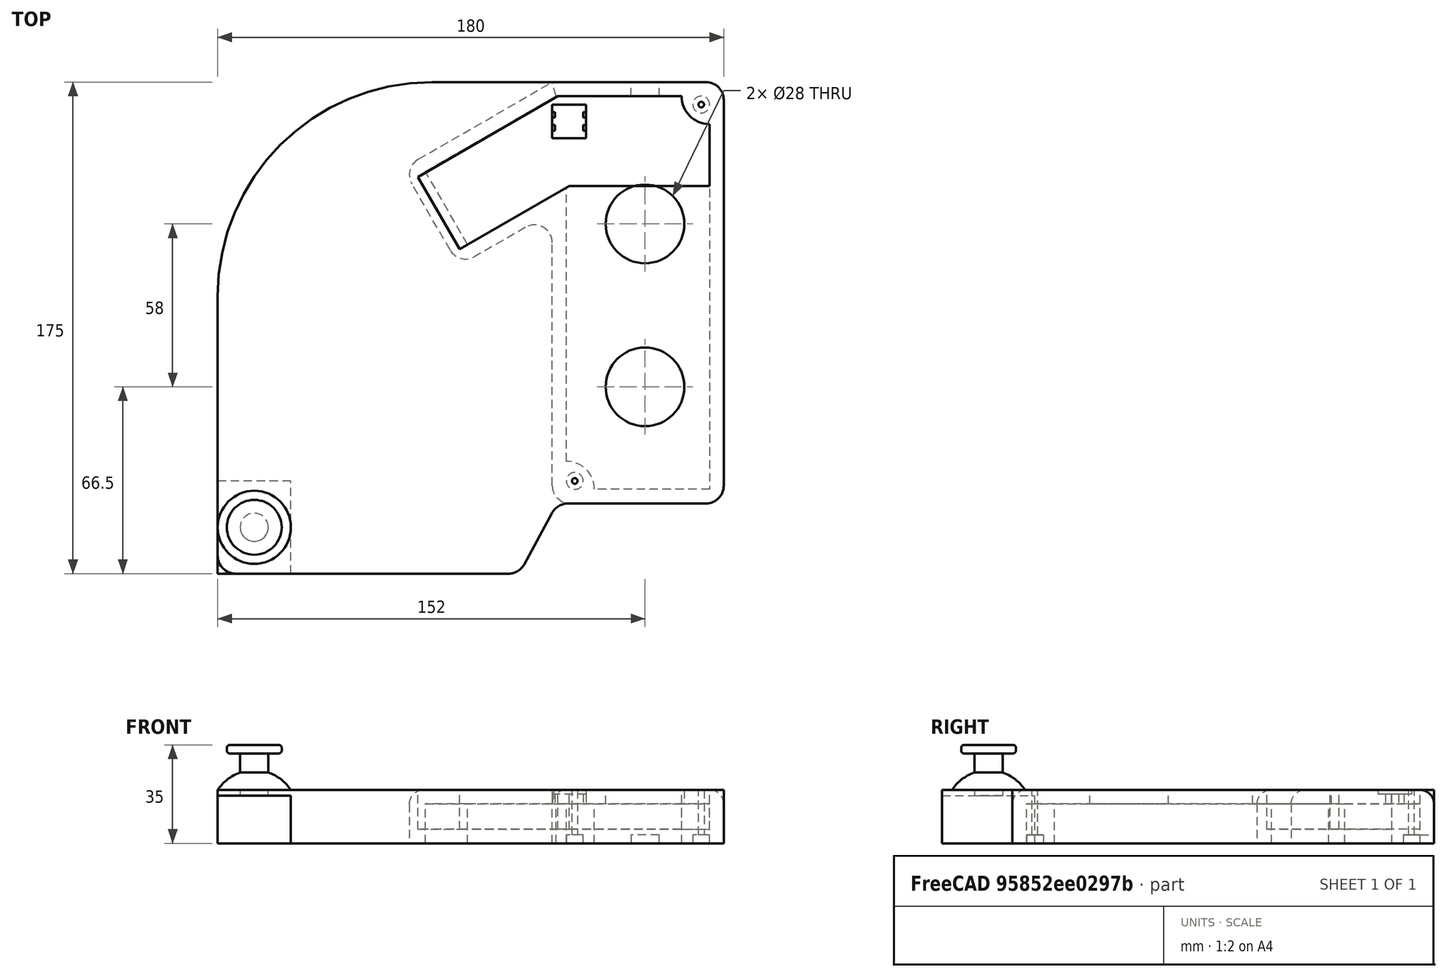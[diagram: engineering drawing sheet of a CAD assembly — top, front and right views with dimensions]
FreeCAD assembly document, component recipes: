
FREECAD ASSEMBLY — COMPONENT RECIPES ("base1")

This assembly document has 3 components, labeled P0..P2 below (a component is one placed body or linked part). 3 of them carry a construction recipe — the FreeCAD feature program that regenerates the part from scratch, quoted from this document or its linked companion documents; the rest are supplied as boundary geometry only. No exploded tour is included for this assembly.
COMPONENT P0 — recipe-attached ("BasePlate", modeled in this document).
Construction recipe (the document's own serialized feature program — sketch geometry with constraints, then the solid features built on it; lengths are millimeters unless a unit is written):

FEATURE [Sketcher::SketchObject] Sketch  label="Base_Ref"
  MapMode = 5
  Support = -> [XY_Plane]
  expr: Constraints[9] = vars.base_l
  expr: Constraints[10] = vars.base_w
  sketch-geometry (4):
    g0: LineSegment StartX=0 StartY=175 StartZ=0 EndX=180 EndY=175 EndZ=0
    g1: LineSegment StartX=180 StartY=175 StartZ=0 EndX=180 EndY=0 EndZ=0
    g2: LineSegment StartX=180 StartY=0 StartZ=0 EndX=0 EndY=0 EndZ=0
    g3: LineSegment StartX=0 StartY=0 StartZ=0 EndX=0 EndY=175 EndZ=0
  constraints (11):
    c: Coincident(g0,g1)
    c: Coincident(g1,g2)
    c: Coincident(g2,g3)
    c: Coincident(g3,g0)
    c: Horizontal(g0)
    c: Horizontal(g2)
    c: Vertical(g1)
    c: Vertical(g3)
    c: Coincident(g2,g-1)
    c: DistanceY(g1,g1) = 175
    c: DistanceX(g0,g0) = 180
FEATURE [Sketcher::SketchObject] Sketch001  label="Base"
  ExternalGeometry = -> [Sketch]
  MapMode = 5
  Support = -> [XY_Plane]
  expr: Constraints[6] = vars.round
  expr: Constraints[10] = vars.round
  expr: Constraints[17] = vars.big_round
  expr: Constraints[22] = vars.round
  expr: Constraints[23] = vars.round
  expr: Constraints[24] = vars.joystick1_margin_out - vars.joystick1_margin_in
  expr: Constraints[25] = vars.joystick1_margin_right + vars.joystick_w + vars.joystick1_margin_left
  sketch-geometry (11):
    g0: LineSegment StartX=180 StartY=175 StartZ=0 EndX=180 EndY=31.35 EndZ=0
    g1: LineSegment StartX=173.65 StartY=25 StartZ=0 EndX=124.577 EndY=25 EndZ=0
    g2: LineSegment StartX=119 StartY=21.6858 StartZ=0 EndX=109 EndY=3.31418 EndZ=0
    g3: LineSegment StartX=103.423 StartY=0 StartZ=0 EndX=6.35 EndY=0 EndZ=0
    g4: ArcOfCircle CenterX=124.577 CenterY=18.65 CenterZ=0 NormalX=0 NormalY=0 NormalZ=1 AngleXU=0 Radius=6.35 StartAngle=1.5708 EndAngle=2.64312
    g5: ArcOfCircle CenterX=103.423 CenterY=6.35 CenterZ=0 NormalX=0 NormalY=0 NormalZ=1 AngleXU=0 Radius=6.35 StartAngle=4.71239 EndAngle=5.78472
    g6: LineSegment StartX=180 StartY=175 StartZ=0 EndX=76.2 EndY=175 EndZ=0
    g7: LineSegment StartX=0 StartY=98.8 StartZ=0 EndX=0 EndY=6.35 EndZ=0
    g8: ArcOfCircle CenterX=76.2 CenterY=98.8 CenterZ=0 NormalX=0 NormalY=0 NormalZ=1 AngleXU=0 Radius=76.2 StartAngle=1.5708 EndAngle=3.14159
    g9: ArcOfCircle CenterX=173.65 CenterY=31.35 CenterZ=0 NormalX=0 NormalY=0 NormalZ=1 AngleXU=0 Radius=6.35 StartAngle=4.71239 EndAngle=6.28319
    g10: ArcOfCircle CenterX=6.35 CenterY=6.35 CenterZ=0 NormalX=0 NormalY=0 NormalZ=1 AngleXU=0 Radius=6.35 StartAngle=3.14159 EndAngle=4.71239
  constraints (27):
    c: Coincident(g-3,g0)
    c: Vertical(g0)
    c: Horizontal(g1)
    c: PointOnObject(g3,g-5)
    c: Tangent(g4,g1) = -1.5708
    c: Tangent(g4,g2) = -1.5708
    c: Radius(g4) = 6.35
    c: PointOnObject(g3,g-5)
    c: Tangent(g5,g2) = 1.5708
    c: Tangent(g5,g3) = 1.5708
    c: Radius(g5) = 6.35
    c: Coincident(g6,g0)
    c: Horizontal(g6)
    c: PointOnObject(g7,g-4)
    c: PointOnObject(g7,g-4)
    c: Tangent(g8,g6) = -1.5708
    c: Tangent(g8,g7) = -1.5708
    c: Radius(g8) = 76.2
    c: Tangent(g9,g0) = 1.5708
    c: Tangent(g9,g1) = 1.5708
    c: Tangent(g10,g3) = 1.5708
    c: Tangent(g10,g7) = -1.5708
    c: Radius(g10) = 6.35
    c: Radius(g9) = 6.35
    c: DistanceY(g-5,g1) = 25
    c: DistanceX(g2,g0) = 61
    c: DistanceX(g2,g2) = 10
FEATURE [PartDesign::Pad] Pad
  Length = 19
  Length2 = 100
  Profile = -> Sketch001
  Type = 0
  expr: Length = vars.base_t
FEATURE [PartDesign::CoordinateSystem] LCS_1
  AttacherType = Attacher::AttachEngine3D
  MapMode = 7
  Placement = pos=(180,0,0) rot=(0,0.707107,0.707107;3.14159rad)
  Support = -> [Sketch]
FEATURE [PartDesign::Fillet] Fillet001
  Base = -> Pad [Edge1]
  BaseFeature = -> Pad
  Radius = 6.35
  SupportTransform = true
  expr: Radius = vars.round
FEATURE [Sketcher::SketchObject] Sketch007
  AttachmentOffset = pos=(0,0,5) rot=(0,0,1;0rad)
  ExternalGeometry = -> [Sketch]
  MapMode = 5
  Placement = pos=(0,0,5) rot=(0,0,1;0rad)
  Support = -> [XY_Plane]
  expr: Constraints[12] = vars.top_wall
  expr: .AttachmentOffset.Base.z = vars.top_wall
  expr: Constraints[11] = vars.top_wall
  expr: Constraints[5] = 22
  expr: Constraints[19] = vars.buttons_angle + 90
  expr: Constraints[20] = 45
  sketch-geometry (7):
    g0: LineSegment StartX=165 StartY=170 StartZ=0 EndX=121 EndY=170 EndZ=0
    g1: LineSegment StartX=125 StartY=138 StartZ=0 EndX=175 EndY=138 EndZ=0
    g2: LineSegment StartX=175 StartY=138 StartZ=0 EndX=175 EndY=160 EndZ=0
    g3: ArcOfCircle CenterX=175 CenterY=170 CenterZ=0 NormalX=0 NormalY=0 NormalZ=1 AngleXU=0 Radius=10 StartAngle=3.14159 EndAngle=4.71239
    g4: LineSegment StartX=121 StartY=170 StartZ=0 EndX=71.1725 EndY=141.232 EndZ=0
    g5: LineSegment StartX=71.1725 StartY=141.232 StartZ=0 EndX=86.0289 EndY=115.5 EndZ=0
    g6: LineSegment StartX=86.0289 StartY=115.5 StartZ=0 EndX=125 EndY=138 EndZ=0
  constraints (22):
    c: Coincident(g1,g2)
    c: Horizontal(g0)
    c: Horizontal(g1)
    c: Vertical(g2)
    c: DistanceX(g1,g1) = 50
    c: DistanceY(g2,g2) = 22
    c: Coincident(g3,g0)
    c: Coincident(g3,g2)
    c: PointOnObject(g3,g0)
    c: PointOnObject(g3,g2)
    c: Radius(g3) = 10
    c: DistanceX(g2,g-3) = 5
    c: DistanceY(g0,g-3) = 5
    c: Coincident(g0,g4)
    c: Coincident(g4,g5)
    c: Coincident(g5,g6)
    c: Coincident(g6,g1)
    c: Parallel(g6,g4)
    c: Perpendicular(g5,g4)
    c: Angle(g4,g0) = 2.61799
    c: Distance(g6) = 45
    c: DistanceX(g0,g0) = 44
FEATURE [PartDesign::Pocket] Pocket002
  BaseFeature = -> Fillet001
  Length = 5
  Length2 = 100
  Profile = -> Sketch007
  Reversed = true
  Type = 1
FEATURE [PartDesign::CoordinateSystem] LCS_7
  AttacherType = Attacher::AttachEngine3D
  MapMode = 7
  Placement = pos=(86.0289,115.5,5) rot=(0.774597,-0.447214,-0.447214;1.82348rad)
  Support = -> [Sketch007]
FEATURE [Sketcher::SketchObject] Sketch014
  ExternalGeometry = -> [Sketch001]
  MapMode = 5
  Support = -> [XY_Plane]
  sketch-geometry (2):
    g0: Circle CenterX=172 CenterY=167 CenterZ=0 NormalX=0 NormalY=0 NormalZ=1 AngleXU=0 Radius=1
    g1: Circle CenterX=127 CenterY=33 CenterZ=0 NormalX=0 NormalY=0 NormalZ=1 AngleXU=0 Radius=1
  constraints (6):
    c: DistanceY(g0,g-4) = 8
    c: DistanceX(g0,g-4) = 8
    c: Radius(g0) = 1
    c: DistanceY(g-5,g1) = 8
    c: DistanceX(g-6,g1) = 8
    c: Equal(g1,g0)
FEATURE [PartDesign::Pocket] Pocket005
  BaseFeature = -> Pocket002
  Length = 5
  Length2 = 100
  Midplane = true
  Profile = -> Sketch014
  Type = 1
FEATURE [Sketcher::SketchObject] Sketch015
  ExternalGeometry = -> [Sketch014]
  MapMode = 5
  Support = -> [XY_Plane]
  sketch-geometry (2):
    g0: Circle CenterX=127 CenterY=33 CenterZ=0 NormalX=0 NormalY=0 NormalZ=1 AngleXU=0 Radius=3
    g1: Circle CenterX=172 CenterY=167 CenterZ=0 NormalX=0 NormalY=0 NormalZ=1 AngleXU=0 Radius=3
  constraints (4):
    c: Coincident(g-4,g0)
    c: Coincident(g1,g-3)
    c: Equal(g1,g0)
    c: Radius(g1) = 3
FEATURE [PartDesign::Pocket] Pocket006
  BaseFeature = -> Pocket005
  Length = 3
  Length2 = 100
  Profile = -> Sketch015
  Reversed = true
  Type = 0
FEATURE [PartDesign::Body] Body  label="BasePlate"
  Group = -> [Sketch,Sketch001,Pad,LCS_1,Fillet001,Sketch007,Pocket002,LCS_7,Sketch014,Pocket005,Sketch015,Pocket006]
  Origin = -> Origin
  Tip = -> Pocket006
COMPONENT P1 — recipe-attached ("TopPlate", modeled in this document).
Construction recipe (the document's own serialized feature program — sketch geometry with constraints, then the solid features built on it; lengths are millimeters unless a unit is written):

FEATURE [Sketcher::SketchObject] Sketch002  label="Base_Ref001"
  MapMode = 5
  Support = -> [XY_Plane001]
  expr: Constraints[10] = vars.base_w
  expr: Constraints[9] = vars.base_l
  sketch-geometry (4):
    g0: LineSegment StartX=0 StartY=175 StartZ=0 EndX=180 EndY=175 EndZ=0
    g1: LineSegment StartX=180 StartY=175 StartZ=0 EndX=180 EndY=0 EndZ=0
    g2: LineSegment StartX=180 StartY=0 StartZ=0 EndX=0 EndY=0 EndZ=0
    g3: LineSegment StartX=0 StartY=0 StartZ=0 EndX=0 EndY=175 EndZ=0
  constraints (11):
    c: Coincident(g0,g1)
    c: Coincident(g1,g2)
    c: Coincident(g2,g3)
    c: Coincident(g3,g0)
    c: Horizontal(g0)
    c: Horizontal(g2)
    c: Vertical(g1)
    c: Vertical(g3)
    c: Coincident(g2,g-1)
    c: DistanceY(g1,g1) = 175
    c: DistanceX(g0,g0) = 180
FEATURE [Sketcher::SketchObject] Sketch003  label="Base001"
  ExternalGeometry = -> [Sketch002]
  MapMode = 5
  Support = -> [XY_Plane001]
  expr: Constraints[25] = vars.joystick1_margin_right + vars.joystick_w + vars.joystick1_margin_left
  expr: Constraints[24] = vars.joystick1_margin_out - vars.joystick1_margin_in
  expr: Constraints[23] = vars.round
  expr: Constraints[22] = vars.round
  expr: Constraints[17] = vars.big_round
  expr: Constraints[10] = vars.round
  expr: Constraints[6] = vars.round
  sketch-geometry (11):
    g0: LineSegment StartX=180 StartY=175 StartZ=0 EndX=180 EndY=31.35 EndZ=0
    g1: LineSegment StartX=173.65 StartY=25 StartZ=0 EndX=124.577 EndY=25 EndZ=0
    g2: LineSegment StartX=119 StartY=21.6858 StartZ=0 EndX=109 EndY=3.31418 EndZ=0
    g3: LineSegment StartX=103.423 StartY=0 StartZ=0 EndX=6.35 EndY=0 EndZ=0
    g4: ArcOfCircle CenterX=124.577 CenterY=18.65 CenterZ=0 NormalX=0 NormalY=0 NormalZ=1 AngleXU=0 Radius=6.35 StartAngle=1.5708 EndAngle=2.64312
    g5: ArcOfCircle CenterX=103.423 CenterY=6.35 CenterZ=0 NormalX=0 NormalY=0 NormalZ=1 AngleXU=0 Radius=6.35 StartAngle=4.71239 EndAngle=5.78472
    g6: LineSegment StartX=180 StartY=175 StartZ=0 EndX=76.2 EndY=175 EndZ=0
    g7: LineSegment StartX=0 StartY=98.8 StartZ=0 EndX=0 EndY=6.35 EndZ=0
    g8: ArcOfCircle CenterX=76.2 CenterY=98.8 CenterZ=0 NormalX=0 NormalY=0 NormalZ=1 AngleXU=0 Radius=76.2 StartAngle=1.5708 EndAngle=3.14159
    g9: ArcOfCircle CenterX=173.65 CenterY=31.35 CenterZ=0 NormalX=0 NormalY=0 NormalZ=1 AngleXU=0 Radius=6.35 StartAngle=4.71239 EndAngle=6.28319
    g10: ArcOfCircle CenterX=6.35 CenterY=6.35 CenterZ=0 NormalX=0 NormalY=0 NormalZ=1 AngleXU=0 Radius=6.35 StartAngle=3.14159 EndAngle=4.71239
  constraints (27):
    c: Coincident(g-3,g0)
    c: Vertical(g0)
    c: Horizontal(g1)
    c: PointOnObject(g3,g-5)
    c: Tangent(g4,g1) = -1.5708
    c: Tangent(g4,g2) = -1.5708
    c: Radius(g4) = 6.35
    c: PointOnObject(g3,g-5)
    c: Tangent(g5,g2) = 1.5708
    c: Tangent(g5,g3) = 1.5708
    c: Radius(g5) = 6.35
    c: Coincident(g6,g0)
    c: Horizontal(g6)
    c: PointOnObject(g7,g-4)
    c: PointOnObject(g7,g-4)
    c: Tangent(g8,g6) = -1.5708
    c: Tangent(g8,g7) = -1.5708
    c: Radius(g8) = 76.2
    c: Tangent(g9,g0) = 1.5708
    c: Tangent(g9,g1) = 1.5708
    c: Tangent(g10,g3) = 1.5708
    c: Tangent(g10,g7) = -1.5708
    c: Radius(g10) = 6.35
    c: Radius(g9) = 6.35
    c: DistanceY(g-5,g1) = 25
    c: DistanceX(g2,g0) = 61
    c: DistanceX(g2,g2) = 10
FEATURE [Sketcher::SketchObject] Sketch004
  ExternalGeometry = -> [Sketch002]
  MapMode = 5
  Support = -> [XY_Plane001]
  expr: Constraints[18] = vars.joystick_sep
  expr: Constraints[19] = vars.joystick1_margin_right
  expr: Constraints[23] = vars.joystick_w
  expr: Constraints[20] = vars.joystick1_margin_out
  expr: Constraints[22] = vars.joystick_l
  expr: Constraints[25] = vars.joystick_w / 2 + 1
  sketch-geometry (11):
    g0: LineSegment [constr] StartX=139 StartY=83 StartZ=0 EndX=165 EndY=83 EndZ=0
    g1: LineSegment [constr] StartX=165 StartY=83 StartZ=0 EndX=165 EndY=50 EndZ=0
    g2: LineSegment [constr] StartX=165 StartY=50 StartZ=0 EndX=139 EndY=50 EndZ=0
    g3: LineSegment [constr] StartX=139 StartY=50 StartZ=0 EndX=139 EndY=83 EndZ=0
    g4: LineSegment [constr] StartX=139 StartY=141 StartZ=0 EndX=165 EndY=141 EndZ=0
    g5: LineSegment [constr] StartX=165 StartY=141 StartZ=0 EndX=165 EndY=108 EndZ=0
    g6: LineSegment [constr] StartX=165 StartY=108 StartZ=0 EndX=139 EndY=108 EndZ=0
    g7: LineSegment [constr] StartX=139 StartY=108 StartZ=0 EndX=139 EndY=141 EndZ=0
    g8: Circle CenterX=152 CenterY=124.5 CenterZ=0 NormalX=0 NormalY=0 NormalZ=1 AngleXU=0 Radius=14
    g9: GeomPoint X=152 Y=66.5 Z=0
    g10: Circle CenterX=152 CenterY=66.5 CenterZ=0 NormalX=0 NormalY=0 NormalZ=1 AngleXU=0 Radius=14
  constraints (29):
    c: Coincident(g0,g1)
    c: Coincident(g1,g2)
    c: Coincident(g2,g3)
    c: Coincident(g3,g0)
    c: Horizontal(g0)
    c: Horizontal(g2)
    c: Vertical(g1)
    c: Vertical(g3)
    c: Coincident(g4,g5)
    c: Coincident(g5,g6)
    c: Coincident(g6,g7)
    c: Coincident(g7,g4)
    c: Horizontal(g4)
    c: Horizontal(g6)
    c: Vertical(g5)
    c: Vertical(g7)
    c: PointOnObject(g6,g3)
    c: PointOnObject(g5,g1)
    c: DistanceY(g0,g5) = 25
    c: DistanceX(g1,g-3) = 15
    c: DistanceY(g-3,g1) = 50
    c: Equal(g5,g1)
    c: DistanceY(g1,g1) = 33
    c: DistanceX(g4,g4) = 26
    c: Symmetric(g5,g4,g8)
    c: Radius(g8) = 14
    c: Symmetric(g0,g1,g9)
    c: Coincident(g10,g9)
    c: Equal(g10,g8)
FEATURE [PartDesign::CoordinateSystem] LCS_2
  AttacherType = Attacher::AttachEngine3D
  MapMode = 7
  Placement = pos=(180,0,0) rot=(0,0.707107,0.707107;3.14159rad)
  Support = -> [Sketch002]
FEATURE [Sketcher::SketchObject] Sketch005
  ExternalGeometry = -> [Sketch002]
  MapMode = 5
  Support = -> [XY_Plane001]
  expr: Constraints[56] = vars.buttons_l
  expr: Constraints[46] = vars.buttons_angle
  expr: Constraints[32] = vars.joystick1_margin_out - vars.joystick1_margin_in
  expr: Constraints[28] = vars.round
  expr: Constraints[55] = vars.buttons_w
  expr: Constraints[22] = vars.joystick_l
  expr: Constraints[20] = vars.joystick1_margin_out
  expr: Constraints[23] = vars.joystick_w
  expr: Constraints[19] = vars.joystick1_margin_right
  expr: Constraints[36] = vars.joystick1_margin_left
  expr: Constraints[18] = vars.joystick_sep
  sketch-geometry (21):
    g0: LineSegment [constr] StartX=139 StartY=83 StartZ=0 EndX=165 EndY=83 EndZ=0
    g1: LineSegment [constr] StartX=165 StartY=83 StartZ=0 EndX=165 EndY=50 EndZ=0
    g2: LineSegment [constr] StartX=165 StartY=50 StartZ=0 EndX=139 EndY=50 EndZ=0
    g3: LineSegment [constr] StartX=139 StartY=50 StartZ=0 EndX=139 EndY=83 EndZ=0
    g4: LineSegment [constr] StartX=139 StartY=141 StartZ=0 EndX=165 EndY=141 EndZ=0
    g5: LineSegment [constr] StartX=165 StartY=141 StartZ=0 EndX=165 EndY=108 EndZ=0
    g6: LineSegment [constr] StartX=165 StartY=108 StartZ=0 EndX=139 EndY=108 EndZ=0
    g7: LineSegment [constr] StartX=139 StartY=108 StartZ=0 EndX=139 EndY=141 EndZ=0
    g8: LineSegment StartX=119 StartY=31.35 StartZ=0 EndX=119 EndY=117.813 EndZ=0
    g9: LineSegment StartX=109.475 StartY=123.313 StartZ=0 EndX=91.3686 EndY=112.859 EndZ=0
    g10: LineSegment StartX=82.6943 StartY=115.183 StartZ=0 EndX=69.0443 EndY=138.826 EndZ=0
    g11: LineSegment StartX=71.3686 StartY=147.5 StartZ=0 EndX=119 EndY=175 EndZ=0
    g12: LineSegment StartX=119 StartY=175 StartZ=0 EndX=173.65 EndY=175 EndZ=0
    g13: LineSegment StartX=180 StartY=168.65 StartZ=0 EndX=180 EndY=31.35 EndZ=0
    g14: LineSegment StartX=173.65 StartY=25 StartZ=0 EndX=125.35 EndY=25 EndZ=0
    g15: ArcOfCircle CenterX=173.65 CenterY=31.35 CenterZ=0 NormalX=0 NormalY=0 NormalZ=1 AngleXU=0 Radius=6.35 StartAngle=4.71239 EndAngle=6.28319
    g16: ArcOfCircle CenterX=125.35 CenterY=31.35 CenterZ=0 NormalX=0 NormalY=0 NormalZ=1 AngleXU=0 Radius=6.35 StartAngle=3.14159 EndAngle=4.71239
    g17: ArcOfCircle CenterX=112.65 CenterY=117.813 CenterZ=0 NormalX=0 NormalY=0 NormalZ=1 AngleXU=0 Radius=6.35 StartAngle=7e-16 EndAngle=2.0944
    g18: ArcOfCircle CenterX=88.1936 CenterY=118.358 CenterZ=0 NormalX=0 NormalY=0 NormalZ=1 AngleXU=0 Radius=6.35 StartAngle=3.66519 EndAngle=5.23599
    g19: ArcOfCircle CenterX=74.5436 CenterY=142.001 CenterZ=0 NormalX=0 NormalY=0 NormalZ=1 AngleXU=0 Radius=6.35 StartAngle=2.0944 EndAngle=3.66519
    g20: ArcOfCircle CenterX=173.65 CenterY=168.65 CenterZ=0 NormalX=0 NormalY=0 NormalZ=1 AngleXU=0 Radius=6.35 StartAngle=3e-16 EndAngle=1.5708
  constraints (57):
    c: Coincident(g0,g1)
    c: Coincident(g1,g2)
    c: Coincident(g2,g3)
    c: Coincident(g3,g0)
    c: Horizontal(g0)
    c: Horizontal(g2)
    c: Vertical(g1)
    c: Vertical(g3)
    c: Coincident(g4,g5)
    c: Coincident(g5,g6)
    c: Coincident(g6,g7)
    c: Coincident(g7,g4)
    c: Horizontal(g4)
    c: Horizontal(g6)
    c: Vertical(g5)
    c: Vertical(g7)
    c: PointOnObject(g6,g3)
    c: PointOnObject(g5,g1)
    c: DistanceY(g0,g5) = 25
    c: DistanceX(g1,g-3) = 15
    c: DistanceY(g-3,g1) = 50
    c: Equal(g5,g1)
    c: DistanceY(g1,g1) = 33
    c: DistanceX(g4,g4) = 26
    c: Vertical(g8)
    c: Horizontal(g12)
    c: Tangent(g15,g13) = 1.5708
    c: Tangent(g15,g14) = 1.5708
    c: Radius(g15) = 6.35
    c: Horizontal(g14)
    c: Vertical(g13)
    c: PointOnObject(g-3,g13)
    c: DistanceY(g-3,g14) = 25
    c: Tangent(g16,g14) = 1.5708
    c: Tangent(g16,g8) = 1.5708
    c: Equal(g16,g15)
    c: DistanceX(g8,g2) = 20
    c: Tangent(g17,g8) = -1.5708
    c: Tangent(g17,g9) = -1.5708
    c: Tangent(g19,g11) = 1.5708
    c: Tangent(g18,g9) = 1.5708
    c: Tangent(g18,g10) = 1.5708
    c: Equal(g16,g17)
    c: Equal(g17,g18)
    c: Equal(g18,g19)
    c: Parallel(g11,g9)
    c: Angle(g9,g8) = 1.0472
    c: Perpendicular(g9,g10)
    c: Tangent(g20,g13) = 1.5708
    c: Tangent(g20,g12) = 1.5708
    c: Equal(g16,g20)
    c: Coincident(g11,g12)
    c: PointOnObject(g11,g8)
    c: PointOnObject(g11,g-4)
    c: Tangent(g10,g19) = 1.5708
    c: Distance(g9,g11) = 40
    c: Distance(g11) = 55
FEATURE [PartDesign::Pad] Pad001
  Length = 19
  Length2 = 100
  Profile = -> Sketch005
  Type = 0
  expr: Length = vars.base_t
FEATURE [PartDesign::Pocket] Pocket
  BaseFeature = -> Pad001
  Length = 5
  Length2 = 100
  Midplane = true
  Profile = -> Sketch004
  Type = 1
FEATURE [Sketcher::SketchObject] Sketch006
  ExternalGeometry = -> [Sketch005]
  MapMode = 5
  Support = -> [XY_Plane001]
  expr: Constraints[11] = vars.top_wall
  expr: Constraints[16] = vars.buttons_w - 2 * vars.top_wall
  expr: Constraints[12] = vars.top_wall
  expr: Constraints[10] = vars.top_wall
  expr: Constraints[32] = vars.top_wall
  sketch-geometry (11):
    g0: LineSegment StartX=73.8686 StartY=143.17 StartZ=0 EndX=120.34 EndY=170 EndZ=0
    g1: LineSegment StartX=120.34 StartY=170 StartZ=0 EndX=165 EndY=170 EndZ=0
    g2: LineSegment StartX=175 StartY=160 StartZ=0 EndX=175 EndY=30 EndZ=0
    g3: LineSegment StartX=175 StartY=30 StartZ=0 EndX=134 EndY=30 EndZ=0
    g4: LineSegment StartX=124 StartY=40 StartZ=0 EndX=124 EndY=137.472 EndZ=0
    g5: LineSegment StartX=124 StartY=137.472 StartZ=0 EndX=88.8686 EndY=117.189 EndZ=0
    g6: LineSegment StartX=88.8686 StartY=117.189 StartZ=0 EndX=73.8686 EndY=143.17 EndZ=0
    g7: LineSegment [constr] StartX=71.3686 StartY=147.5 StartZ=0 EndX=73.8686 EndY=143.17 EndZ=0
    g8: LineSegment [constr] StartX=88.8686 StartY=117.189 StartZ=0 EndX=91.3686 EndY=112.859 EndZ=0
    g9: ArcOfCircle CenterX=175 CenterY=170 CenterZ=0 NormalX=0 NormalY=0 NormalZ=1 AngleXU=0 Radius=10 StartAngle=3.14159 EndAngle=4.71239
    g10: ArcOfCircle CenterX=124 CenterY=30 CenterZ=0 NormalX=0 NormalY=0 NormalZ=1 AngleXU=0 Radius=10 StartAngle=-9e-16 EndAngle=1.5708
  constraints (33):
    c: Coincident(g0,g1)
    c: Horizontal(g1)
    c: Vertical(g2)
    c: Coincident(g2,g3)
    c: Vertical(g4)
    c: Coincident(g4,g5)
    c: Coincident(g5,g6)
    c: Parallel(g-3,g3)
    c: Parallel(g5,g-8)
    c: Parallel(g6,g-9)
    c: DistanceY(g-3,g2) = 5
    c: DistanceX(g2,g-5) = 5
    c: DistanceY(g1,g-6) = 5
    c: Coincident(g0,g6)
    c: Parallel(g0,g-7)
    c: PointOnObject(g-7,g6)
    c: Distance(g6) = 30
    c: Coincident(g7,g-7)
    c: Coincident(g7,g0)
    c: Coincident(g8,g5)
    c: Coincident(g8,g-8)
    c: Equal(g8,g7)
    c: Coincident(g9,g1)
    c: Coincident(g9,g2)
    c: Radius(g9) = 10
    c: PointOnObject(g9,g1)
    c: PointOnObject(g9,g2)
    c: Coincident(g10,g4)
    c: Coincident(g10,g3)
    c: Equal(g9,g10)
    c: PointOnObject(g10,g4)
    c: PointOnObject(g10,g3)
    c: DistanceX(g-4,g10) = 5
FEATURE [PartDesign::Pocket] Pocket001
  BaseFeature = -> Pocket
  Length = 14
  Length2 = 100
  Profile = -> Sketch006
  Reversed = true
  Type = 0
  expr: Length = vars.base_t - vars.top_wall
FEATURE [PartDesign::Fillet] Fillet
  Base = -> Pocket001 [Edge31]
  BaseFeature = -> Pocket001
  Radius = 5
  SupportTransform = true
  expr: Radius = vars.fillet
FEATURE [PartDesign::CoordinateSystem] LCS_6
  AttacherType = Attacher::AttachEngine3D
  MapMode = 11
  Placement = pos=(152,66.5,0) rot=(0,0,1;1.5708rad)
  Support = -> [Sketch004]
FEATURE [PartDesign::CoordinateSystem] LCS_8
  AttacherType = Attacher::AttachEngine3D
  MapMode = 11
  Placement = pos=(152,124.5,0) rot=(0,0,1;1.5708rad)
  Support = -> [Sketch004]
FEATURE [Sketcher::SketchObject] Sketch012
  AttachmentOffset = pos=(0,0,19) rot=(0,0,1;0rad)
  ExternalGeometry = -> [Sketch003]
  MapMode = 5
  Placement = pos=(0,0,19) rot=(0,0,1;0rad)
  Support = -> [XY_Plane001]
  expr: Constraints[9] = vars.push_size
  expr: Constraints[10] = vars.fillet + 3
  expr: Constraints[11] = vars.joystick1_margin_left + vars.joystick_w + vars.joystick1_margin_right - vars.push_size
  expr: .AttachmentOffset.Base.z = vars.base_t
  sketch-geometry (4):
    g0: LineSegment StartX=119 StartY=167 StartZ=0 EndX=131 EndY=167 EndZ=0
    g1: LineSegment StartX=131 StartY=167 StartZ=0 EndX=131 EndY=155 EndZ=0
    g2: LineSegment StartX=131 StartY=155 StartZ=0 EndX=119 EndY=155 EndZ=0
    g3: LineSegment StartX=119 StartY=155 StartZ=0 EndX=119 EndY=167 EndZ=0
  constraints (12):
    c: Coincident(g0,g1)
    c: Coincident(g1,g2)
    c: Coincident(g2,g3)
    c: Coincident(g3,g0)
    c: Horizontal(g0)
    c: Horizontal(g2)
    c: Vertical(g1)
    c: Vertical(g3)
    c: Equal(g0,g3)
    c: DistanceY(g1,g1) = 12
    c: DistanceY(g0,g-4) = 8
    c: DistanceX(g0,g-4) = 49
FEATURE [PartDesign::Pocket] Pocket003
  BaseFeature = -> Fillet
  Length = 3
  Length2 = 100
  Midplane = true
  Profile = -> Sketch012
  Reversed = true
  Type = 0
FEATURE [Sketcher::SketchObject] Sketch013
  AttachmentOffset = pos=(0,0,19) rot=(0,0,1;0rad)
  ExternalGeometry = -> [Sketch012]
  MapMode = 5
  Placement = pos=(0,0,19) rot=(0,0,1;0rad)
  Support = -> [XY_Plane001]
  expr: .AttachmentOffset.Base.z = vars.base_t
  sketch-geometry (19):
    g0: LineSegment StartX=119 StartY=164.333 StartZ=0 EndX=120 EndY=164.333 EndZ=0
    g1: LineSegment StartX=120 StartY=164.333 StartZ=0 EndX=120 EndY=162.333 EndZ=0
    g2: LineSegment StartX=120 StartY=162.333 StartZ=0 EndX=119 EndY=162.333 EndZ=0
    g3: LineSegment StartX=119 StartY=162.333 StartZ=0 EndX=119 EndY=164.333 EndZ=0
    g4: LineSegment StartX=130 StartY=164.333 StartZ=0 EndX=131 EndY=164.333 EndZ=0
    g5: LineSegment StartX=131 StartY=164.333 StartZ=0 EndX=131 EndY=162.333 EndZ=0
    g6: LineSegment StartX=131 StartY=162.333 StartZ=0 EndX=130 EndY=162.333 EndZ=0
    g7: LineSegment StartX=130 StartY=162.333 StartZ=0 EndX=130 EndY=164.333 EndZ=0
    g8: LineSegment StartX=119 StartY=159.667 StartZ=0 EndX=120 EndY=159.667 EndZ=0
    g9: LineSegment StartX=120 StartY=159.667 StartZ=0 EndX=120 EndY=157.667 EndZ=0
    g10: LineSegment StartX=120 StartY=157.667 StartZ=0 EndX=119 EndY=157.667 EndZ=0
    g11: LineSegment StartX=119 StartY=157.667 StartZ=0 EndX=119 EndY=159.667 EndZ=0
    g12: LineSegment StartX=130 StartY=159.667 StartZ=0 EndX=131 EndY=159.667 EndZ=0
    g13: LineSegment StartX=131 StartY=159.667 StartZ=0 EndX=131 EndY=157.667 EndZ=0
    g14: LineSegment StartX=131 StartY=157.667 StartZ=0 EndX=130 EndY=157.667 EndZ=0
    g15: LineSegment StartX=130 StartY=157.667 StartZ=0 EndX=130 EndY=159.667 EndZ=0
    g16: LineSegment [constr] StartX=131 StartY=167 StartZ=0 EndX=131 EndY=164.333 EndZ=0
    g17: LineSegment [constr] StartX=131 StartY=162.333 StartZ=0 EndX=131 EndY=159.667 EndZ=0
    g18: LineSegment [constr] StartX=131 StartY=157.667 StartZ=0 EndX=131 EndY=155 EndZ=0
  constraints (54):
    c: Coincident(g0,g1)
    c: Coincident(g1,g2)
    c: Coincident(g2,g3)
    c: Coincident(g3,g0)
    c: Horizontal(g0)
    c: Horizontal(g2)
    c: Vertical(g1)
    c: Vertical(g3)
    c: Coincident(g4,g5)
    c: Coincident(g5,g6)
    c: Coincident(g6,g7)
    c: Coincident(g7,g4)
    c: Horizontal(g4)
    c: Horizontal(g6)
    c: Vertical(g5)
    c: Vertical(g7)
    c: Coincident(g8,g9)
    c: Coincident(g9,g10)
    c: Coincident(g10,g11)
    c: Coincident(g11,g8)
    c: Horizontal(g8)
    c: Horizontal(g10)
    c: Vertical(g9)
    c: Vertical(g11)
    c: Coincident(g12,g13)
    c: Coincident(g13,g14)
    c: Coincident(g14,g15)
    c: Coincident(g15,g12)
    c: Horizontal(g12)
    c: Horizontal(g14)
    c: Vertical(g13)
    c: Vertical(g15)
    c: Equal(g1,g7)
    c: Equal(g7,g9)
    c: Equal(g9,g15)
    c: Equal(g0,g4)
    c: Equal(g4,g8)
    c: Equal(g8,g12)
    c: PointOnObject(g13,g-4)
    c: PointOnObject(g5,g-4)
    c: PointOnObject(g2,g-6)
    c: PointOnObject(g10,g-6)
    c: PointOnObject(g8,g12)
    c: PointOnObject(g0,g4)
    c: DistanceX(g8,g8) = 1
    c: Coincident(g16,g-4)
    c: Coincident(g16,g4)
    c: Coincident(g17,g5)
    c: Coincident(g17,g12)
    c: Coincident(g18,g13)
    c: Coincident(g18,g-5)
    c: Equal(g16,g17)
    c: Equal(g17,g18)
    c: DistanceY(g1,g1) = 2
FEATURE [PartDesign::Pocket] Pocket004
  BaseFeature = -> Pocket003
  Length = 5
  Length2 = 100
  Midplane = true
  Profile = -> Sketch013
  Type = 1
FEATURE [Sketcher::SketchObject] Sketch016
  AttachmentOffset = pos=(0,0,-100) rot=(0,0,1;0rad)
  MapMode = 5
  Placement = pos=(0,100,2.22e-14) rot=(1,0,0;1.5708rad)
  Support = -> [XZ_Plane001]
  sketch-geometry (4):
    g0: LineSegment StartX=147 StartY=3 StartZ=0 EndX=157 EndY=3 EndZ=0
    g1: LineSegment StartX=157 StartY=3 StartZ=0 EndX=157 EndY=0 EndZ=0
    g2: LineSegment StartX=157 StartY=0 StartZ=0 EndX=147 EndY=0 EndZ=0
    g3: LineSegment StartX=147 StartY=0 StartZ=0 EndX=147 EndY=3 EndZ=0
  constraints (12):
    c: Coincident(g0,g1)
    c: Coincident(g1,g2)
    c: Coincident(g2,g3)
    c: Coincident(g3,g0)
    c: Horizontal(g0)
    c: Horizontal(g2)
    c: Vertical(g1)
    c: Vertical(g3)
    c: PointOnObject(g2,g-1)
    c: DistanceY(g1,g1) = 3
    c: DistanceX(g0,g0) = 10
    c: DistanceX(g-1,g2) = 147
FEATURE [PartDesign::Pocket] Pocket007
  BaseFeature = -> Pocket004
  Length = 5
  Length2 = 100
  Profile = -> Sketch016
  Type = 1
FEATURE [PartDesign::Body] Body001  label="TopPlate"
  Group = -> [Sketch002,Sketch003,Sketch004,LCS_2,Sketch005,Pad001,Pocket,Sketch006,Pocket001,Fillet,LCS_6,LCS_8,Sketch012,Pocket003,Sketch013,Pocket004,Sketch016,Pocket007]
  Origin = -> Origin001
  Tip = -> Pocket007
COMPONENT P2 — recipe-attached ("Joystick", modeled in this document).
Construction recipe (the document's own serialized feature program — sketch geometry with constraints, then the solid features built on it; lengths are millimeters unless a unit is written):

FEATURE [Sketcher::SketchObject] Sketch008
  MapMode = 5
  Support = -> [XY_Plane003]
  expr: Constraints[9] = vars.joystick_l
  expr: Constraints[10] = vars.joystick_w
  sketch-geometry (4):
    g0: LineSegment StartX=0 StartY=0 StartZ=0 EndX=26 EndY=0 EndZ=0
    g1: LineSegment StartX=26 StartY=0 StartZ=0 EndX=26 EndY=33 EndZ=0
    g2: LineSegment StartX=26 StartY=33 StartZ=0 EndX=0 EndY=33 EndZ=0
    g3: LineSegment StartX=0 StartY=33 StartZ=0 EndX=0 EndY=0 EndZ=0
  constraints (11):
    c: Coincident(g0,g1)
    c: Coincident(g1,g2)
    c: Coincident(g2,g3)
    c: Coincident(g3,g0)
    c: Horizontal(g0)
    c: Horizontal(g2)
    c: Vertical(g1)
    c: Vertical(g3)
    c: Coincident(g0,g-1)
    c: DistanceY(g1,g1) = 33
    c: DistanceX(g0,g0) = 26
FEATURE [PartDesign::Pad] Pad002
  Length = 17
  Length2 = 100
  Profile = -> Sketch008
  Type = 0
  expr: Length = vars.joystick_h1
FEATURE [Sketcher::SketchObject] Sketch009
  MapMode = 5
  Support = -> [XY_Plane003]
  expr: Constraints[0] = vars.joystick_l / 2
  expr: Constraints[1] = vars.joystick_w / 2
  sketch-geometry (1):
    g0: Circle CenterX=13 CenterY=16.5 CenterZ=0 NormalX=0 NormalY=0 NormalZ=1 AngleXU=0 Radius=5
  constraints (3):
    c: DistanceY(g-1,g0) = 16.5
    c: DistanceX(g-1,g0) = 13
    c: Radius(g0) = 5
FEATURE [PartDesign::Pad] Pad003
  BaseFeature = -> Pad002
  Length = 34
  Length2 = 100
  Profile = -> Sketch009
  Type = 0
  expr: Length = vars.joystick_h2 - 1
FEATURE [Sketcher::SketchObject] Sketch010
  AttachmentOffset = pos=(13,2,-16.5) rot=(0,0,1;0rad)
  MapMode = 5
  Placement = pos=(13,16.5,2) rot=(1,0,0;1.5708rad)
  Support = -> [XZ_Plane003]
  expr: .AttachmentOffset.Base.x = vars.joystick_w / 2
  expr: Constraints[5] = vars.joystick_h1
  expr: .AttachmentOffset.Base.z = -vars.joystick_l / 2
  expr: Constraints[7] = vars.joystick_w / 2
  sketch-geometry (3):
    g0: LineSegment StartX=0 StartY=24 StartZ=0 EndX=0 EndY=17 EndZ=0
    g1: LineSegment StartX=0 StartY=17 StartZ=0 EndX=-13 EndY=17 EndZ=0
    g2: ArcOfCircle CenterX=0 CenterY=8.42857 CenterZ=0 NormalX=0 NormalY=0 NormalZ=1 AngleXU=0 Radius=15.5714 StartAngle=1.5708 EndAngle=2.55868
  constraints (10):
    c: Vertical(g0)
    c: Coincident(g1,g0)
    c: Horizontal(g1)
    c: Coincident(g2,g0)
    c: Coincident(g2,g1)
    c: DistanceY(g-1,g0) = 17
    c: PointOnObject(g2,g0)
    c: DistanceX(g1,g1) = 13
    c: DistanceY(g0,g0) = 7
    c: PointOnObject(g0,g-2)
FEATURE [PartDesign::Revolution] Revolution
  Angle = 360
  Axis = (0,-2e-16,1)
  Base = (13,16.5,2)
  BaseFeature = -> Pad003
  Profile = -> Sketch010
  ReferenceAxis = -> Sketch010 [V_Axis]
FEATURE [Sketcher::SketchObject] Sketch011
  AttachmentOffset = pos=(0,0,33.5) rot=(0,0,1;0rad)
  MapMode = 5
  Placement = pos=(0,0,33.5) rot=(0,0,1;0rad)
  Support = -> [XY_Plane003]
  expr: .AttachmentOffset.Base.z = vars.joystick_h2 - 1.5
  expr: Constraints[2] = vars.joystick_w / 2 * 0.75
  expr: Constraints[1] = vars.joystick_w / 2
  expr: Constraints[0] = vars.joystick_l / 2
  sketch-geometry (1):
    g0: Circle CenterX=13 CenterY=16.5 CenterZ=0 NormalX=0 NormalY=0 NormalZ=1 AngleXU=0 Radius=9.75
  constraints (3):
    c: DistanceY(g-1,g0) = 16.5
    c: DistanceX(g-1,g0) = 13
    c: Radius(g0) = 9.75
FEATURE [PartDesign::Pad] Pad004
  BaseFeature = -> Revolution
  Length = 3
  Length2 = 100
  Midplane = true
  Profile = -> Sketch011
  Type = 0
FEATURE [PartDesign::Fillet] Fillet002
  Base = -> Pad004 [Edge25]
  BaseFeature = -> Pad004
  Radius = 1
  SupportTransform = true
FEATURE [PartDesign::Fillet] Fillet003
  Base = -> Fillet002 [Edge3]
  BaseFeature = -> Fillet002
  Radius = 1
  SupportTransform = true
FEATURE [PartDesign::CoordinateSystem] LCS_3
  AttacherType = Attacher::AttachEngine3D
  MapMode = 7
  Placement = pos=(26,0,0) rot=(0,0.707107,0.707107;3.14159rad)
  Support = -> [Sketch008]
FEATURE [PartDesign::CoordinateSystem] LCS_4
  AttacherType = Attacher::AttachEngine3D
  MapMode = 11
  Placement = pos=(13,16.5,0) rot=(0,0,1;1.5708rad)
  Support = -> [Sketch009]
FEATURE [PartDesign::Body] Body002  label="Joystick"
  Group = -> [Sketch008,Pad002,Sketch009,Pad003,Sketch010,Revolution,Sketch011,Pad004,Fillet002,Fillet003,LCS_3,LCS_4]
  Origin = -> Origin003
  Tip = -> Fillet003
PROVENANCE & LICENSES
A FreeCAD (.FCStd) document from a public repository crawl; recipes are the document's own serialized feature recipes (and, for linked parts, companion documents' recipes).
License: gpl-3.0.
